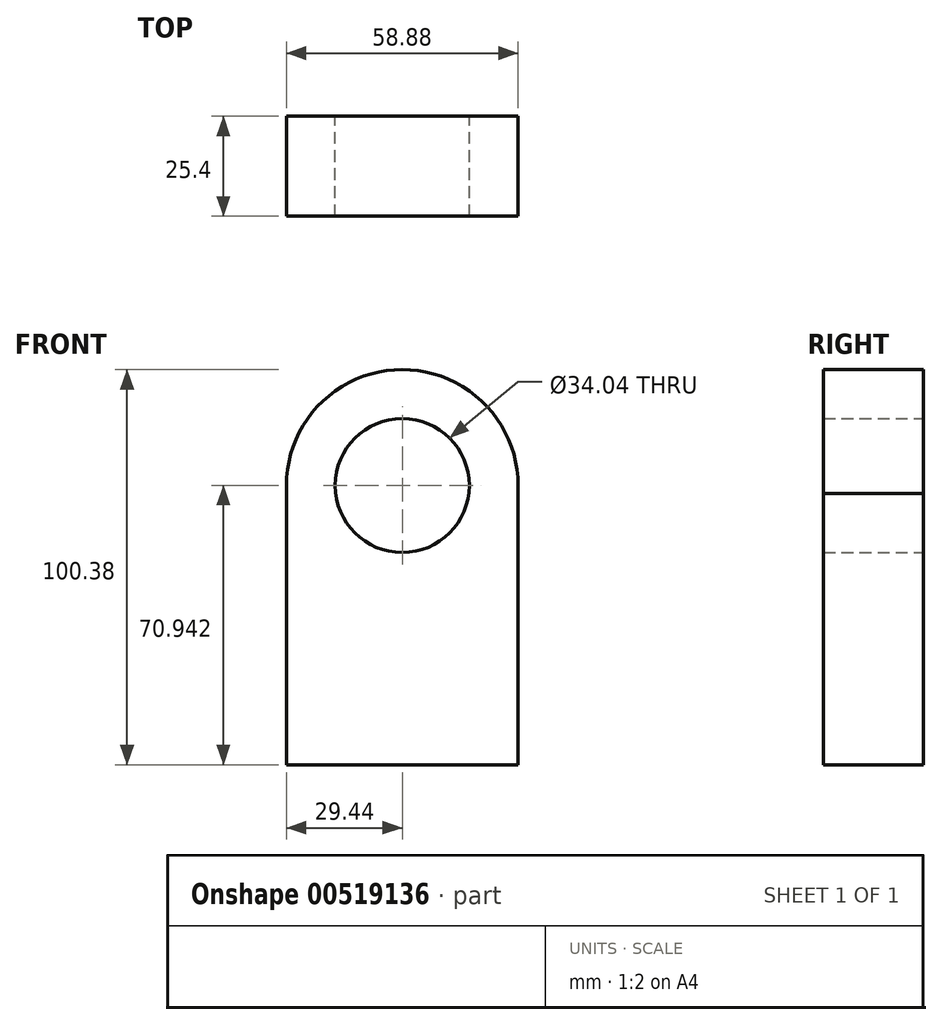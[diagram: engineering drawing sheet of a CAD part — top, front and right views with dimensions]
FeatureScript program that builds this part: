
annotation { "Feature Type Name" : "Feature", "Feature Type Description" : "" }
export const myFeature = defineFeature(function(context is Context, id is Id, definition is map)
    precondition{}
    {
        {
            var Q0;
            Q0=qCreatedBy(makeId("Front.planeOp"),FACE);
            var sketch = newSketch(context, id + "F0", { "sketchPlane" : qUnion([Q0])});
            skLineSegment(sketch, "E0.bottom", {"start": v(29.36, -35.47) * mm, "end": v(-29.36, -35.47) * mm});
            skLineSegment(sketch, "E0.top", {"start": v(29.36, 35.47) * mm, "end": v(-29.36, 35.47) * mm});
            skLineSegment(sketch, "E0.left", {"start": v(29.36, -35.47) * mm, "end": v(29.36, 35.47) * mm});
            skLineSegment(sketch, "E0.right", {"start": v(-29.36, -35.47) * mm, "end": v(-29.36, 35.47) * mm});
            skPoint(sketch, "E0.middle", {"position": v(0, 0) * mm});
            skCircle(sketch, "E1", {"center": v(0, 35.47) * mm, "radius": 29.44 * mm});
            skCircle(sketch, "E2", {"center": v(0, 35.47) * mm, "radius": 17.02 * mm});
            skSolve(sketch);
        }
        {
            var Q0;
            {var subQ1=sQuery(id+"F0.wireOp",EDGE,"E0.top");var subQ5=sQuery(id+"F0.wireOp",EDGE,"E0.left");var subQ6=makeQuery(id+"F0.imprint","INTERSECT",VERTEX,{"derivedFrom":[subQ1,subQ5]});Q0=makeQuery(id+"F0.imprint","IMPRINT",FACE,{"disambiguationData":[TD([[makeQuery(id+"F0.imprint","IMPRINT",EDGE,{"disambiguationData":[TD([[subQ6,-1.0]])],"derivedFrom":subQ1}),1.0]])]});}
            var Q1;
            {var subQ0=sQuery(id+"F0.wireOp",EDGE,"E0.bottom");Q1=makeQuery(id+"F0.imprint","IMPRINT",FACE,{"disambiguationData":[TD([[makeQuery(id+"F0.imprint","IMPRINT",EDGE,{"derivedFrom":subQ0}),-1.0]])]});}
            var Q2;
            {var subQ1=sQuery(id+"F0.wireOp",EDGE,"E0.top");var subQ5=sQuery(id+"F0.wireOp",EDGE,"E0.left");var subQ6=makeQuery(id+"F0.imprint","INTERSECT",VERTEX,{"derivedFrom":[subQ1,subQ5]});Q2=makeQuery(id+"F0.imprint","IMPRINT",FACE,{"disambiguationData":[TD([[makeQuery(id+"F0.imprint","IMPRINT",EDGE,{"disambiguationData":[TD([[subQ6,-1.0]])],"derivedFrom":subQ1}),-1.0]])]});}
            extrude(context, id + "F1", {"entities" : qUnion([Q0, Q1, Q2]), "depth" : 25.4 * mm});
        }
    });
